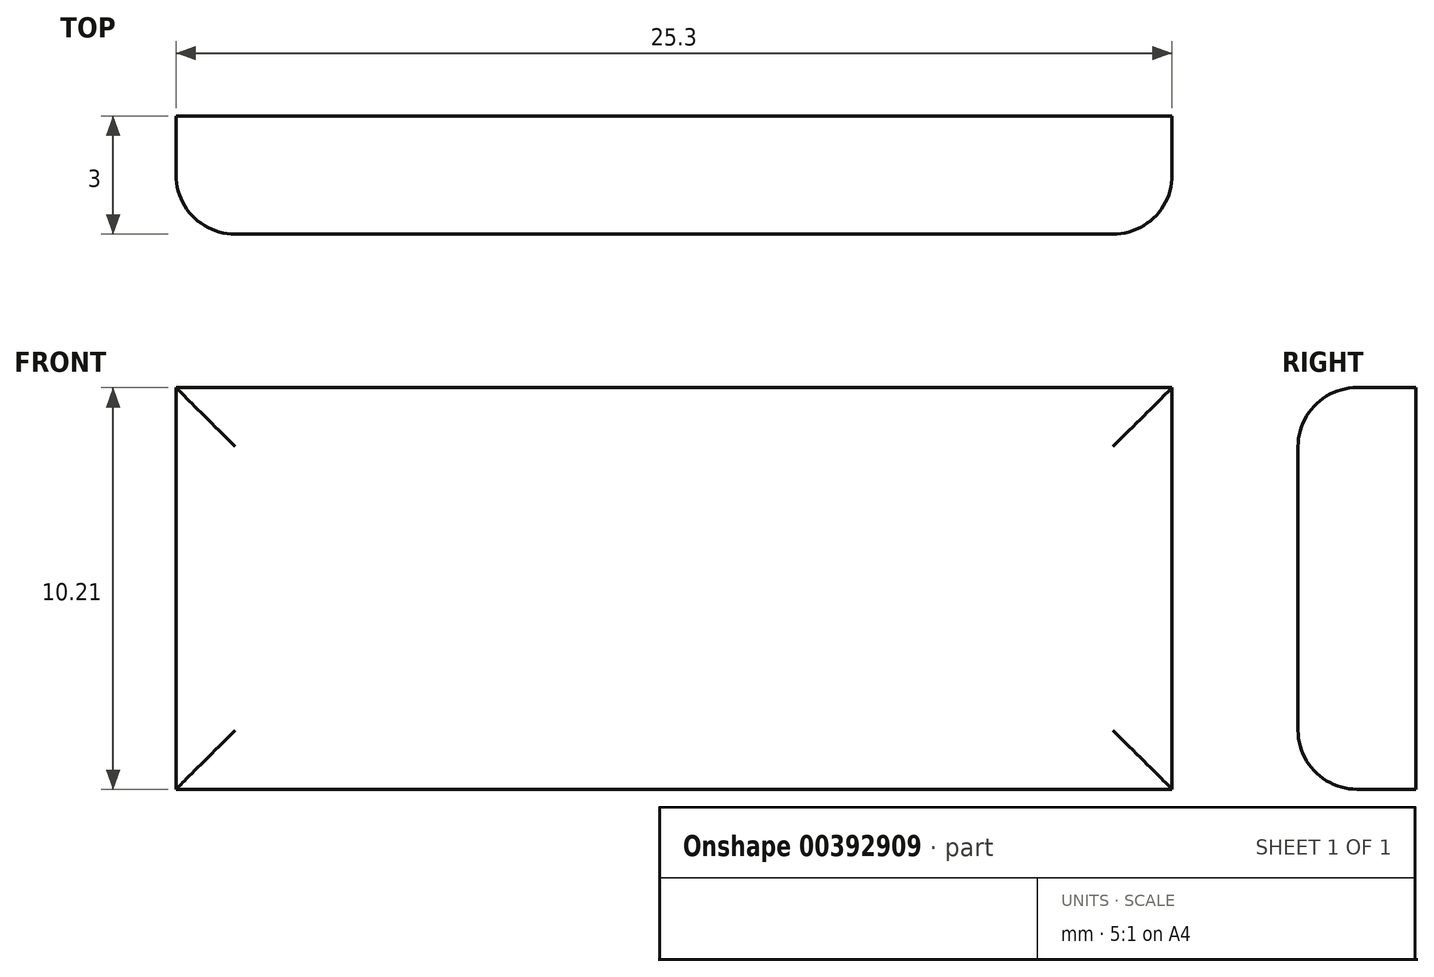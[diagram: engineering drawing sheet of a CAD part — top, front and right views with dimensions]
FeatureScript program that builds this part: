
annotation { "Feature Type Name" : "Feature", "Feature Type Description" : "" }
export const myFeature = defineFeature(function(context is Context, id is Id, definition is map)
    precondition{}
    {
        {
            var Q0;
            Q0=qCreatedBy(makeId("Front.planeOp"),FACE);
            var sketch = newSketch(context, id + "F0", { "sketchPlane" : qUnion([Q0])});
            skText(sketch, "E0", { "text": "-", "fontName": "NotoSerif-Bold.ttf"});
            const initialGuessF0  = {"E0": [0, 0, 1, 0, 0.07]};
            skSetInitialGuess(sketch, initialGuessF0);
            skSolve(sketch);
        }
        {
            var Q0;
            Q0 = qSketchRegion(id + "F0", true);
            extrude(context, id + "F1", {"entities" : qUnion([Q0]), "depth" : 3 * mm});
        }
        {
            var Q0;
            Q0=makeQuery(id+"F1.opExtrude","CAP_FACE",FACE,{"disambiguationData":[OSD([sQuery(id+"F0.wireOp",EDGE,"E0.sketch_text.stroke-0"),sQuery(id+"F0.wireOp",EDGE,"E0.sketch_text.stroke-1"),sQuery(id+"F0.wireOp",EDGE,"E0.sketch_text.stroke-2"),sQuery(id+"F0.wireOp",EDGE,"E0.sketch_text.stroke-3")])],"isStart":false});
            fillet(context, id + "F2", {"entities" : qUnion([Q0]), "radius" : 1.5 * mm, "tangentPropagation" : true, "allowEdgeOverflow" : false});
        }
    });
